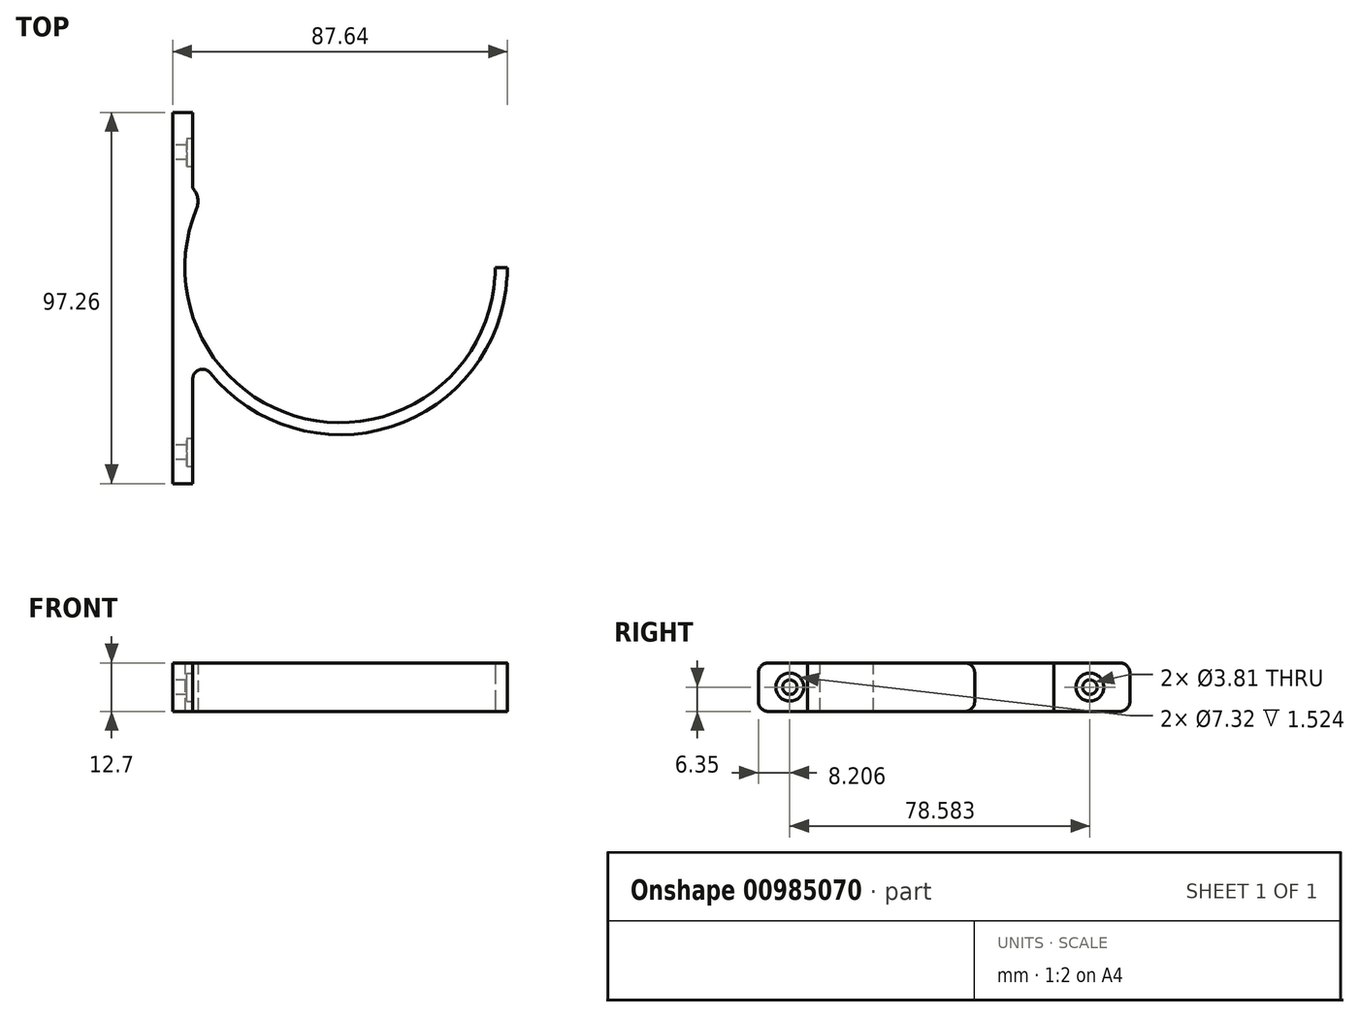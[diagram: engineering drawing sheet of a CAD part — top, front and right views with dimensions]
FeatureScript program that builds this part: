
annotation { "Feature Type Name" : "Feature", "Feature Type Description" : "" }
export const myFeature = defineFeature(function(context is Context, id is Id, definition is map)
    precondition{}
    {
        {
            var Q0;
            Q0=qCreatedBy(makeId("Top.planeOp"),FACE);
            var sketch = newSketch(context, id + "F0", { "sketchPlane" : qUnion([Q0])});
            skArc(sketch, "E0", {"start": v(-35.77, 19.3) * mm, "mid": v(-9.95, -39.4) * mm, "end": v(40.64, 0) * mm});
            skArc(sketch, "E1", {"start": v(-38.56, -20.8) * mm, "mid": v(10.73, -42.48) * mm, "end": v(43.82, 0) * mm});
            skLineSegment(sketch, "E2", {"start": v(-43.81, -43.82) * mm, "end": v(-43.82, 40.64) * mm});
            skLineSegment(sketch, "E3", {"start": v(-43.82, 40.64) * mm, "end": v(-38.56, 40.64) * mm});
            skLineSegment(sketch, "E4", {"start": v(-38.56, 40.64) * mm, "end": v(-38.56, 20.8) * mm});
            skLineSegment(sketch, "E5", {"start": v(-38.56, -43.82) * mm, "end": v(-38.56, -20.8) * mm});
            skLineSegment(sketch, "E6", {"start": v(-38.56, 20.8) * mm, "end": v(-35.77, 19.3) * mm});
            skLineSegment(sketch, "E7", {"start": v(40.64, 0) * mm, "end": v(43.82, 0) * mm});
            skLineSegment(sketch, "E8", {"start": v(-38.56, -43.82) * mm, "end": v(25.94, -43.82) * mm, "construction": true});
            skLineSegment(sketch, "E9", {"start": v(-43.81, -43.82) * mm, "end": v(-43.81, -56.62) * mm});
            skLineSegment(sketch, "E10", {"start": v(-43.81, -56.62) * mm, "end": v(-38.56, -56.62) * mm});
            skLineSegment(sketch, "E11", {"start": v(-38.56, -56.62) * mm, "end": v(-38.56, -43.82) * mm});
            skSolve(sketch);
        }
        {
            var Q0;
            Q0 = qSketchRegion(id + "F0", true);
            extrude(context, id + "F1", {"entities" : qUnion([Q0]), "endBound" : BoundingType.SYMMETRIC, "depth" : 12.7 * mm, "offsetDistance" : 25.4 * mm});
        }
        {
            var Q0;
            Q0=makeQuery(id+"F1.opExtrude","CAP_EDGE",EDGE,{"disambiguationData":[OSD([sQuery(id+"F0.wireOp",EDGE,"E7")])],"isStart":false});
            var Q1;
            Q1=makeQuery(id+"F1.opExtrude","CAP_EDGE",EDGE,{"disambiguationData":[OSD([sQuery(id+"F0.wireOp",EDGE,"E7")])],"isStart":true});
            var Q2;
            Q2=makeQuery(id+"F1.opExtrude","SWEPT_EDGE",EDGE,{"disambiguationData":[OSD([sQuery(id+"F0.wireOp",EDGE,"E1"),sQuery(id+"F0.wireOp",EDGE,"E5")])]});
            var Q3;
            Q3=makeQuery(id+"F1.opExtrude","CAP_EDGE",EDGE,{"disambiguationData":[OSD([sQuery(id+"F0.wireOp",EDGE,"UGx28AVN-NF2L-50kM-4M1Q-ANiipM0NmXr8")])],"isStart":true});
            var Q4;
            Q4=makeQuery(id+"F1.opExtrude","CAP_EDGE",EDGE,{"disambiguationData":[OSD([sQuery(id+"F0.wireOp",EDGE,"UGx28AVN-NF2L-50kM-4M1Q-ANiipM0NmXr8")])],"isStart":false});
            var Q5;
            Q5=makeQuery(id+"F1.opExtrude","CAP_EDGE",EDGE,{"disambiguationData":[OSD([sQuery(id+"F0.wireOp",EDGE,"E3")])],"isStart":false});
            var Q6;
            Q6=makeQuery(id+"F1.opExtrude","CAP_EDGE",EDGE,{"disambiguationData":[OSD([sQuery(id+"F0.wireOp",EDGE,"E3")])],"isStart":true});
            var Q7;
            Q7=makeQuery(id+"F1.opExtrude","CAP_EDGE",EDGE,{"disambiguationData":[OSD([sQuery(id+"F0.wireOp",EDGE,"E10")])],"isStart":false});
            var Q8;
            Q8=makeQuery(id+"F1.opExtrude","CAP_EDGE",EDGE,{"disambiguationData":[OSD([sQuery(id+"F0.wireOp",EDGE,"E10")])],"isStart":true});
            fillet(context, id + "F2", {"entities" : qUnion([Q0, Q1, Q2, Q3, Q4, Q5, Q6, Q7, Q8]), "radius" : 2.54 * mm, "tangentPropagation" : true, "allowEdgeOverflow" : false});
        }
        {
            var Q0;
            Q0=makeQuery(id+"F1.opExtrude","SWEPT_FACE",FACE,{"disambiguationData":[OSD([sQuery(id+"F0.wireOp",EDGE,"E2")])]});
            var sketch = newSketch(context, id + "F3", { "sketchPlane" : qUnion([Q0])});
            skCircle(sketch, "E12", {"center": v(-30.17, 0) * mm, "radius": 1.9 * mm});
            skCircle(sketch, "E13", {"center": v(48.41, 0) * mm, "radius": 1.9 * mm});
            skSolve(sketch);
        }
        {
            var Q0;
            Q0 = qSketchRegion(id + "F3", true);
            extrude(context, id + "F4", {"entities" : qUnion([Q0]), "operationType" : NewBodyOperationType.REMOVE, "oppositeDirection" : true, "depth" : 25.4 * mm, "offsetDistance" : 25.4 * mm});
        }
        {
            var Q0;
            Q0=makeQuery(id+"F1.opExtrude","SWEPT_FACE",FACE,{"disambiguationData":[OSD([sQuery(id+"F0.wireOp",EDGE,"E4")])]});
            var sketch = newSketch(context, id + "F5", { "sketchPlane" : qUnion([Q0])});
            skCircle(sketch, "E14", {"center": v(30.17, 0) * mm, "radius": 3.66 * mm});
            skCircle(sketch, "E15", {"center": v(-48.41, 0) * mm, "radius": 3.66 * mm});
            skSolve(sketch);
        }
        {
            var Q0;
            Q0 = qSketchRegion(id + "F5", true);
            extrude(context, id + "F6", {"entities" : qUnion([Q0]), "operationType" : NewBodyOperationType.REMOVE, "oppositeDirection" : true, "depth" : 1.52 * mm, "offsetDistance" : 25.4 * mm});
        }
        {
            var Q0;
            Q0=makeQuery(id+"F1.opExtrude","SWEPT_EDGE",EDGE,{"disambiguationData":[OSD([sQuery(id+"F0.wireOp",EDGE,"E0"),sQuery(id+"F0.wireOp",EDGE,"E6")])]});
            fillet(context, id + "F7", {"entities" : qUnion([Q0]), "radius" : 5.08 * mm, "tangentPropagation" : true, "allowEdgeOverflow" : false});
        }
    });
